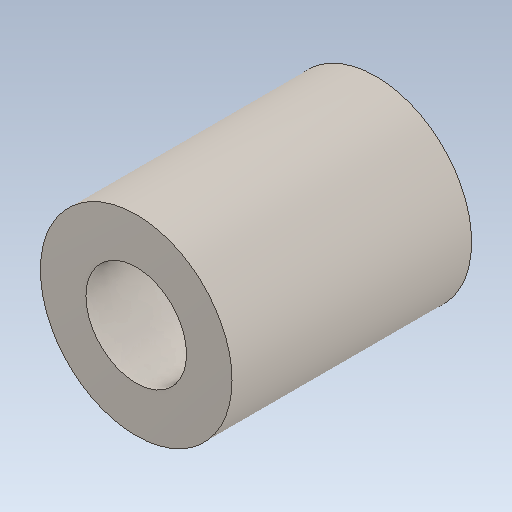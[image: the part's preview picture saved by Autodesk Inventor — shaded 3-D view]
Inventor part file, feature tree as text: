
AUTODESK INVENTOR PART (.ipt)
format: ipt  version: 2021 (Build 250183000, 183)  size: 108,544 bytes
history: native  units: in
note: dims shown in document units (in); Inventor stores cm internally (conversion verified against a paired STEP export)
features: extrude x1
ambient origin geometry x8: Origin, YZ Plane, XZ Plane, XY Plane, X Axis, Y Axis, Z Axis, Center Point
bodies: Solid1 (feature_tree)
feature tree (1):
  extrude  "Extrude1"  [1 undecoded]
note: 1 required parameter value undecoded (feature->parameter linkage not recoverable at this tier; creation-order binding heuristic only, values carry confidence <= 0.55)
